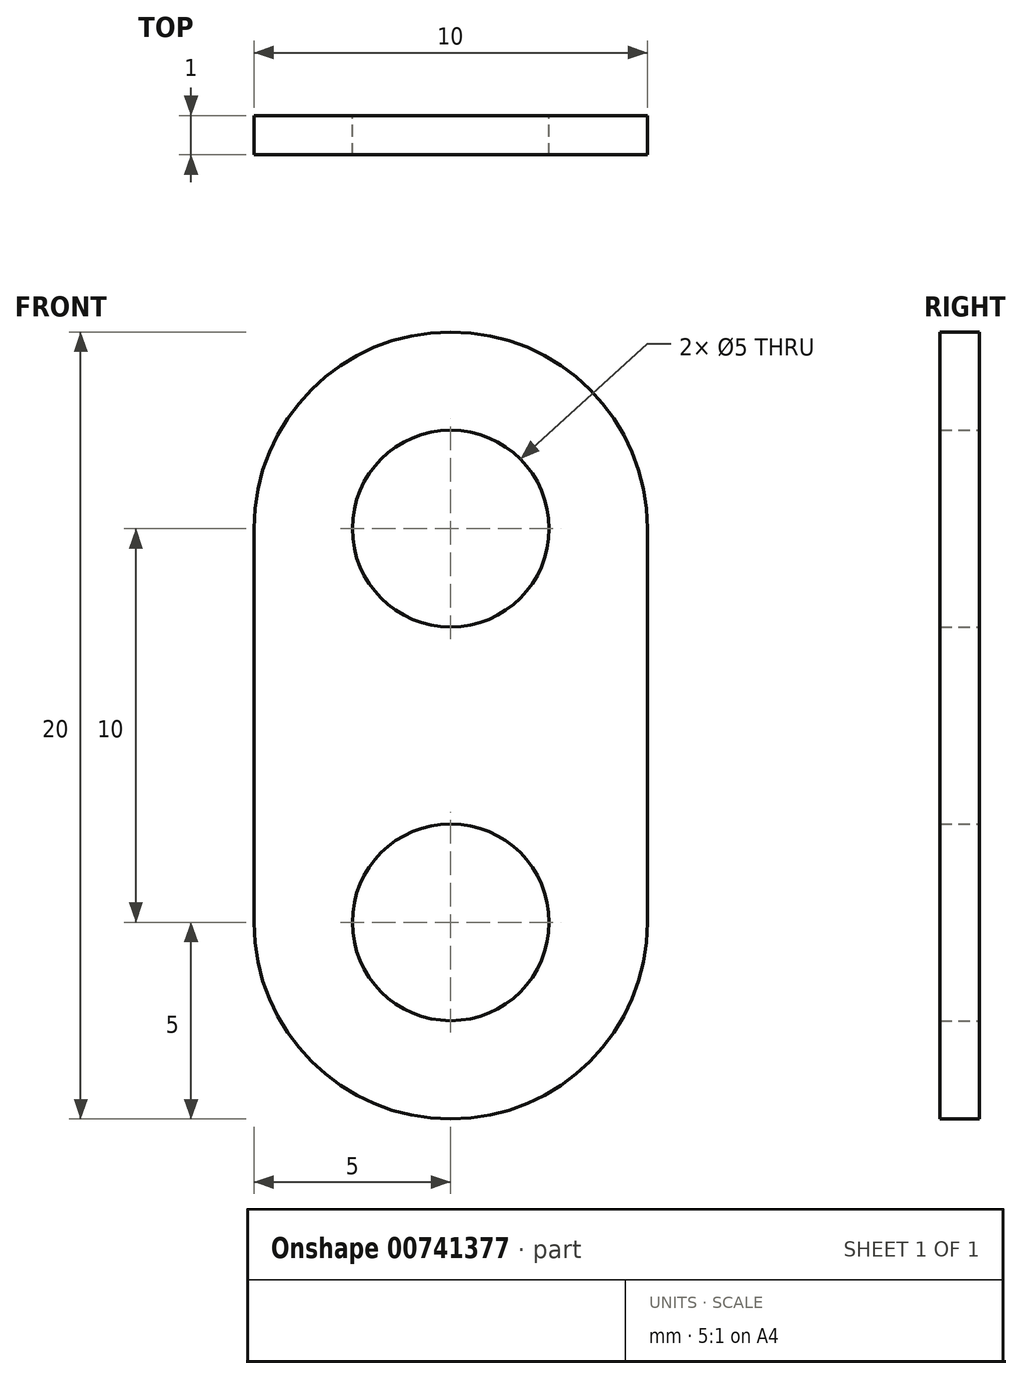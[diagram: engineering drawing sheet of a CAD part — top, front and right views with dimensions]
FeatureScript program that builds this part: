
annotation { "Feature Type Name" : "Feature", "Feature Type Description" : "" }
export const myFeature = defineFeature(function(context is Context, id is Id, definition is map)
    precondition{}
    {
        {
            var Q0;
            Q0=qCreatedBy(makeId("Front.planeOp"),FACE);
            var sketch = newSketch(context, id + "F0", { "sketchPlane" : qUnion([Q0])});
            skCircle(sketch, "E0", {"center": v(0, 5) * mm, "radius": 5 * mm});
            skCircle(sketch, "E1", {"center": v(0, 5) * mm, "radius": 2.5 * mm});
            skLineSegment(sketch, "E2", {"start": v(-27, 0) * mm, "end": v(32.83, 0) * mm, "construction": true});
            skCircle(sketch, "E3.MirrorC", {"center": v(0, -5) * mm, "radius": 5 * mm});
            skCircle(sketch, "E4.MirrorC", {"center": v(0, -5) * mm, "radius": 2.5 * mm});
            skLineSegment(sketch, "E5", {"start": v(-5, -5) * mm, "end": v(-5, 5) * mm});
            skLineSegment(sketch, "E6", {"start": v(5, 5) * mm, "end": v(5, -5) * mm});
            skSolve(sketch);
        }
        {
            var Q0;
            Q0 = qSketchRegion(id + "F0", true);
            extrude(context, id + "F1", {"entities" : qUnion([Q0]), "depth" : 1 * mm, "offsetDistance" : 25 * mm});
        }
    });
